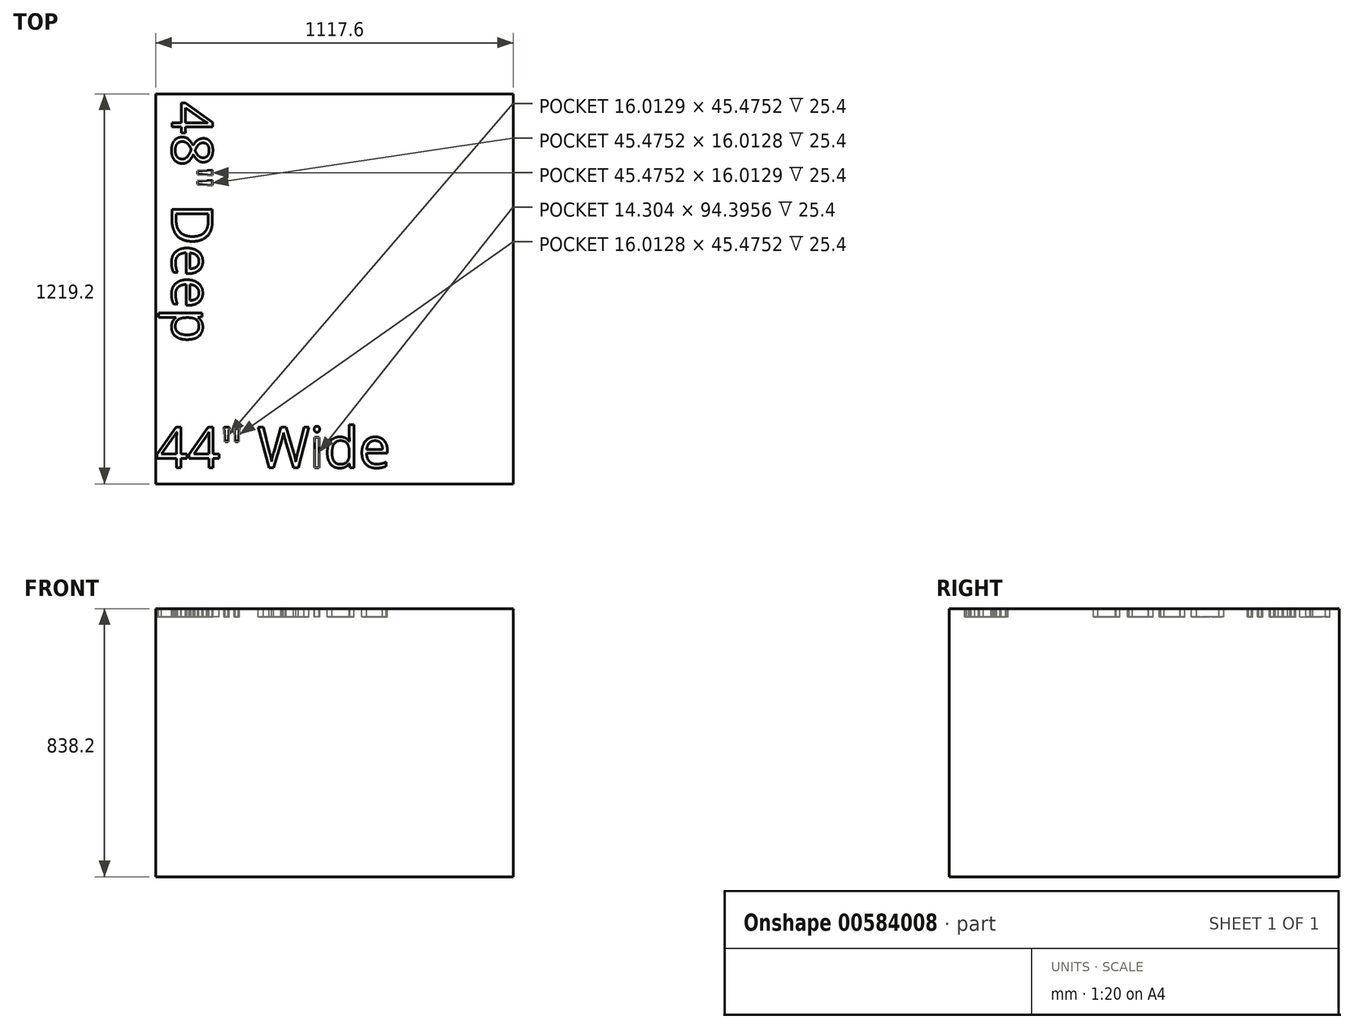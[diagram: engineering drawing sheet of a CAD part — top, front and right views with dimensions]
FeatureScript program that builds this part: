
annotation { "Feature Type Name" : "Feature", "Feature Type Description" : "" }
export const myFeature = defineFeature(function(context is Context, id is Id, definition is map)
    precondition{}
    {
        {
            var Q0;
            Q0=qCreatedBy(makeId("Top.planeOp"),FACE);
            var sketch = newSketch(context, id + "F0", { "sketchPlane" : qUnion([Q0])});
            skLineSegment(sketch, "E0.bottom", {"start": v(-558.8, 609.6) * mm, "end": v(558.8, 609.6) * mm});
            skLineSegment(sketch, "E0.top", {"start": v(-558.8, -609.6) * mm, "end": v(558.8, -609.6) * mm});
            skLineSegment(sketch, "E0.left", {"start": v(-558.8, 609.6) * mm, "end": v(-558.8, -609.6) * mm});
            skLineSegment(sketch, "E0.right", {"start": v(558.8, 609.6) * mm, "end": v(558.8, -609.6) * mm});
            skSolve(sketch);
        }
        {
            var Q0;
            Q0=makeQuery(id+"F0.imprint","IMPRINT",FACE,{"disambiguationData":[TD([[makeQuery(id+"F0.imprint","IMPRINT",EDGE,{"derivedFrom":sQuery(id+"F0.wireOp",EDGE,"E0.bottom")}),-1.0]])]});
            extrude(context, id + "F1", {"entities" : qUnion([Q0]), "depth" : 838.2 * mm, "offsetDistance" : 25.4 * mm});
        }
        {
            var Q0;
            Q0=makeQuery(id+"F1.opExtrude","CAP_FACE",FACE,{"disambiguationData":[OSD([sQuery(id+"F0.wireOp",EDGE,"E0.bottom"),sQuery(id+"F0.wireOp",EDGE,"E0.top"),sQuery(id+"F0.wireOp",EDGE,"E0.left"),sQuery(id+"F0.wireOp",EDGE,"E0.right")])],"isStart":false});
            var sketch = newSketch(context, id + "F2", { "sketchPlane" : qUnion([Q0])});
            skText(sketch, "E1", { "text": "44\" Wide", "fontName": "OpenSans-Regular.ttf"});
            skText(sketch, "E2", { "text": "48\" Deep", "fontName": "OpenSans-Regular.ttf"});
            const initialGuessF2  = {"E1": [-0.5588, -0.5588, 1, 0, 0.127], "E2": [-0.508, 0.5842, 0, -1, 0.127]};
            skSetInitialGuess(sketch, initialGuessF2);
            skSolve(sketch);
        }
        {
            var Q0;
            Q0 = qSketchRegion(id + "F2", true);
            extrude(context, id + "F3", {"entities" : qUnion([Q0]), "operationType" : NewBodyOperationType.REMOVE, "oppositeDirection" : true, "depth" : 25.4 * mm, "offsetDistance" : 25.4 * mm});
        }
    });
